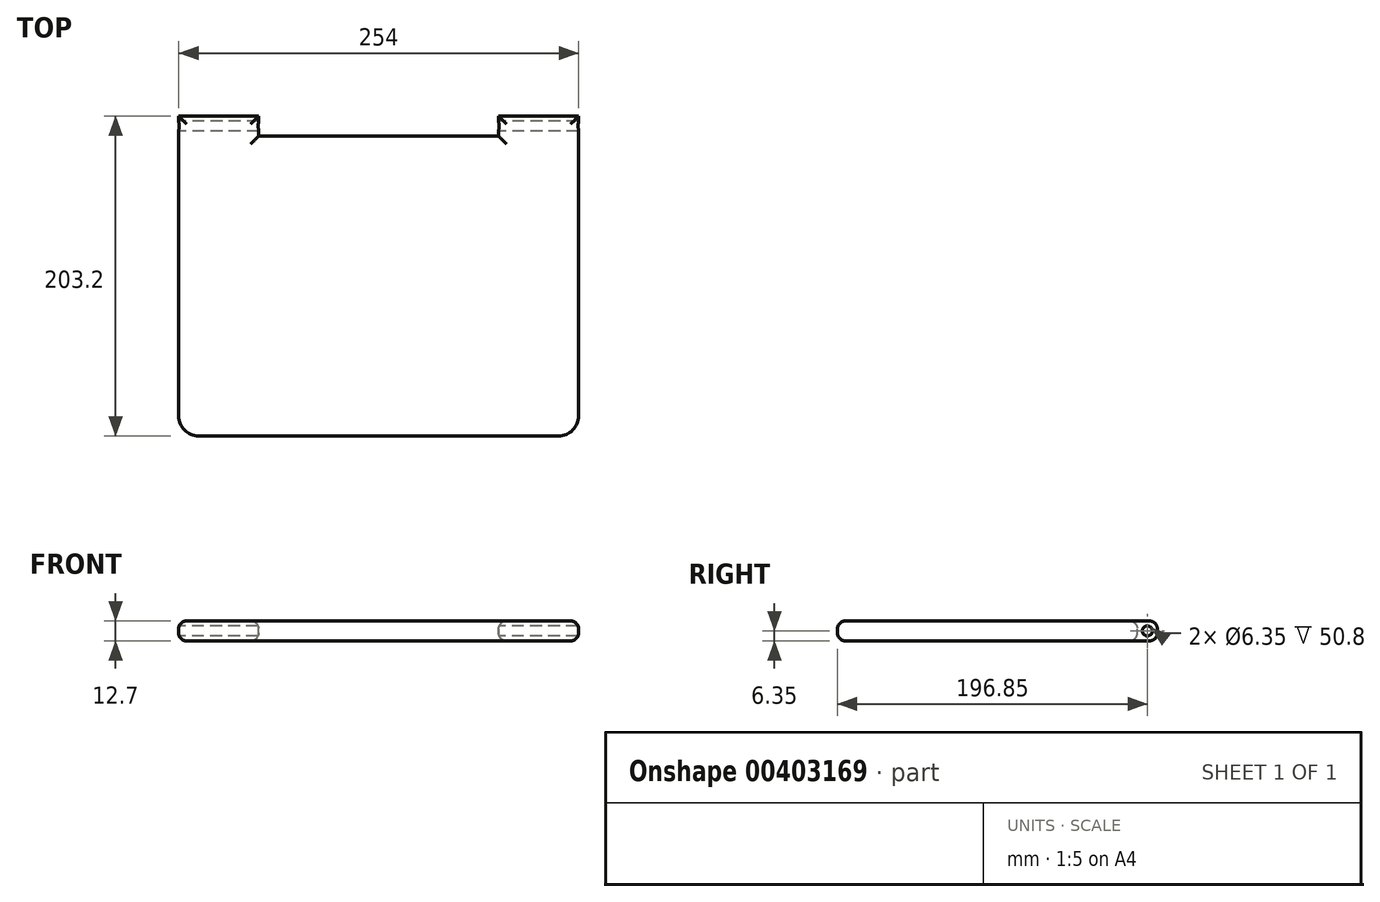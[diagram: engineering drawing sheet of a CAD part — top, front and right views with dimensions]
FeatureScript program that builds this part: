
annotation { "Feature Type Name" : "Feature", "Feature Type Description" : "" }
export const myFeature = defineFeature(function(context is Context, id is Id, definition is map)
    precondition{}
    {
        {
            var Q0;
            Q0=qCreatedBy(makeId("Top.planeOp"),FACE);
            var sketch = newSketch(context, id + "F0", { "sketchPlane" : qUnion([Q0])});
            skLineSegment(sketch, "E0.bottom", {"start": v(-127, 101.6) * mm, "end": v(127, 101.6) * mm});
            skLineSegment(sketch, "E0.top", {"start": v(-127, -101.6) * mm, "end": v(127, -101.6) * mm});
            skLineSegment(sketch, "E0.left", {"start": v(-127, 101.6) * mm, "end": v(-127, -101.6) * mm});
            skLineSegment(sketch, "E0.right", {"start": v(127, 101.6) * mm, "end": v(127, -101.6) * mm});
            skPoint(sketch, "E0.middle", {"position": v(0, 0) * mm});
            skSolve(sketch);
        }
        {
            var Q0;
            Q0=makeQuery(id+"F0.imprint","IMPRINT",FACE,{"disambiguationData":[TD([[makeQuery(id+"F0.imprint","IMPRINT",EDGE,{"derivedFrom":sQuery(id+"F0.wireOp",EDGE,"E0.bottom")}),-1.0]])]});
            extrude(context, id + "F1", {"entities" : qUnion([Q0]), "depth" : 12.7 * mm});
        }
        {
            var Q0;
            Q0=makeQuery(id+"F1.opExtrude","CAP_FACE",FACE,{"disambiguationData":[OSD([sQuery(id+"F0.wireOp",EDGE,"E0.bottom"),sQuery(id+"F0.wireOp",EDGE,"E0.top"),sQuery(id+"F0.wireOp",EDGE,"E0.left"),sQuery(id+"F0.wireOp",EDGE,"E0.right")])],"isStart":false});
            var sketch = newSketch(context, id + "F2", { "sketchPlane" : qUnion([Q0])});
            skLineSegment(sketch, "E1.bottom", {"start": v(-76.2, 101.6) * mm, "end": v(-127, 101.6) * mm});
            skLineSegment(sketch, "E1.top", {"start": v(-76.2, 88.9) * mm, "end": v(-127, 88.9) * mm});
            skLineSegment(sketch, "E1.left", {"start": v(-76.2, 101.6) * mm, "end": v(-76.2, 88.9) * mm});
            skLineSegment(sketch, "E1.right", {"start": v(-127, 101.6) * mm, "end": v(-127, 88.9) * mm});
            skLineSegment(sketch, "E2", {"start": v(0, 101.6) * mm, "end": v(0, -101.6) * mm});
            skLineSegment(sketch, "E3.MirrorCS", {"start": v(127, 101.6) * mm, "end": v(127, 88.9) * mm});
            skLineSegment(sketch, "E4.MirrorCS", {"start": v(76.2, 101.6) * mm, "end": v(76.2, 88.9) * mm});
            skLineSegment(sketch, "E5.MirrorCS", {"start": v(76.2, 88.9) * mm, "end": v(127, 88.9) * mm});
            skLineSegment(sketch, "E6.MirrorCS", {"start": v(76.2, 101.6) * mm, "end": v(127, 101.6) * mm});
            skLineSegment(sketch, "E7", {"start": v(-76.2, 88.9) * mm, "end": v(76.2, 88.9) * mm});
            skLineSegment(sketch, "E8", {"start": v(76.2, 101.6) * mm, "end": v(-76.2, 101.6) * mm});
            skSolve(sketch);
        }
        {
            var Q0;
            Q0=makeQuery(id+"F1.opExtrude","SWEPT_FACE",FACE,{"disambiguationData":[OSD([sQuery(id+"F0.wireOp",EDGE,"E0.left")])]});
            var sketch = newSketch(context, id + "F3", { "sketchPlane" : qUnion([Q0])});
            skLineSegment(sketch, "E9", {"start": v(-101.6, 6.35) * mm, "end": v(-86.85, 6.35) * mm});
            skCircle(sketch, "E10", {"center": v(-95.25, 6.35) * mm, "radius": 3.18 * mm});
            skSolve(sketch);
        }
        {
            var Q0;
            Q0=qSketchRegion(id+"F3",true);
            extrude(context, id + "F4", {"entities" : qUnion([Q0]), "operationType" : NewBodyOperationType.REMOVE, "endBound" : BoundingType.THROUGH_ALL, "oppositeDirection" : true, "depth" : 25.4 * mm});
        }
        {
            var Q0;
            {var subQ0=sQuery(id+"F2.wireOp",EDGE,"E1.left");Q0=makeQuery(id+"F2.imprint","IMPRINT",FACE,{"disambiguationData":[TD([[makeQuery(id+"F2.imprint","IMPRINT",EDGE,{"derivedFrom":subQ0}),1.0]])]});}
            var Q1;
            {var subQ5=sQuery(id+"F2.wireOp",EDGE,"E4.MirrorCS");Q1=makeQuery(id+"F2.imprint","IMPRINT",FACE,{"disambiguationData":[TD([[makeQuery(id+"F2.imprint","IMPRINT",EDGE,{"derivedFrom":subQ5}),-1.0]])]});}
            extrude(context, id + "F5", {"entities" : qUnion([Q0, Q1]), "operationType" : NewBodyOperationType.REMOVE, "endBound" : BoundingType.THROUGH_ALL, "oppositeDirection" : true, "depth" : 25.4 * mm});
        }
        {
            var Q0;
            Q0=makeQuery(id+"F1.opExtrude","CAP_FACE",FACE,{"disambiguationData":[OSD([sQuery(id+"F0.wireOp",EDGE,"E0.bottom"),sQuery(id+"F0.wireOp",EDGE,"E0.top"),sQuery(id+"F0.wireOp",EDGE,"E0.left"),sQuery(id+"F0.wireOp",EDGE,"E0.right")])],"isStart":false});
            var Q1;
            Q1=makeQuery(id+"F1.opExtrude","CAP_FACE",FACE,{"disambiguationData":[OSD([sQuery(id+"F0.wireOp",EDGE,"E0.bottom"),sQuery(id+"F0.wireOp",EDGE,"E0.top"),sQuery(id+"F0.wireOp",EDGE,"E0.left"),sQuery(id+"F0.wireOp",EDGE,"E0.right")])],"isStart":true});
            fillet(context, id + "F6", {"entities" : qUnion([Q0, Q1]), "radius" : 5.08 * mm, "tangentPropagation" : true, "allowEdgeOverflow" : false});
        }
        {
            var Q0;
            Q0=makeQuery(id+"F1.opExtrude","SWEPT_EDGE",EDGE,{"disambiguationData":[OSD([sQuery(id+"F0.wireOp",EDGE,"E0.top"),sQuery(id+"F0.wireOp",EDGE,"E0.left")])]});
            var Q1;
            Q1=makeQuery(id+"F1.opExtrude","SWEPT_EDGE",EDGE,{"disambiguationData":[OSD([sQuery(id+"F0.wireOp",EDGE,"E0.top"),sQuery(id+"F0.wireOp",EDGE,"E0.right")])]});
            fillet(context, id + "F7", {"entities" : qUnion([Q0, Q1]), "radius" : 12.7 * mm, "tangentPropagation" : true, "allowEdgeOverflow" : false});
        }
    });
